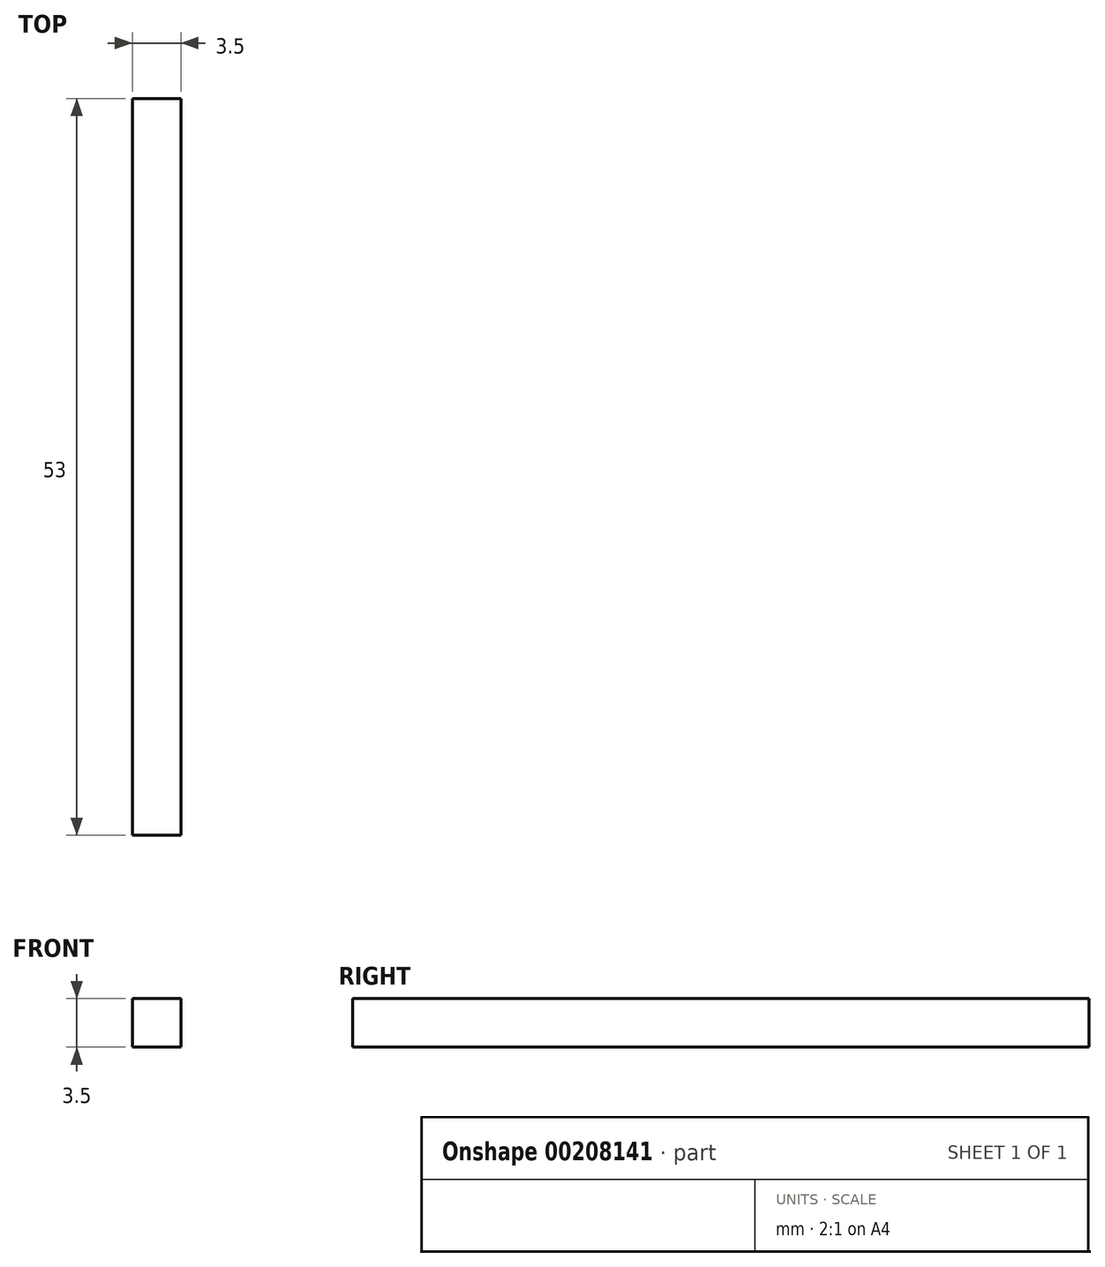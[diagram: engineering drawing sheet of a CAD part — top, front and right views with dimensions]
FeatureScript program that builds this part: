
annotation { "Feature Type Name" : "Feature", "Feature Type Description" : "" }
export const myFeature = defineFeature(function(context is Context, id is Id, definition is map)
    precondition{}
    {
        {
            var Q0;
            Q0=qCreatedBy(makeId("Top.planeOp"),FACE);
            var sketch = newSketch(context, id + "F0", { "sketchPlane" : qUnion([Q0])});
            skLineSegment(sketch, "E0.bottom", {"start": v(1.75, 26.5) * mm, "end": v(-1.75, 26.5) * mm});
            skLineSegment(sketch, "E0.top", {"start": v(1.75, -26.5) * mm, "end": v(-1.75, -26.5) * mm});
            skLineSegment(sketch, "E0.left", {"start": v(1.75, 26.5) * mm, "end": v(1.75, -26.5) * mm});
            skLineSegment(sketch, "E0.right", {"start": v(-1.75, 26.5) * mm, "end": v(-1.75, -26.5) * mm});
            skPoint(sketch, "E0.middle", {"position": v(0, 0) * mm});
            skSolve(sketch);
        }
        {
            var Q0;
            Q0 = qSketchRegion(id + "F0", true);
            extrude(context, id + "F1", {"entities" : qUnion([Q0]), "depth" : 3.5 * mm});
        }
    });
